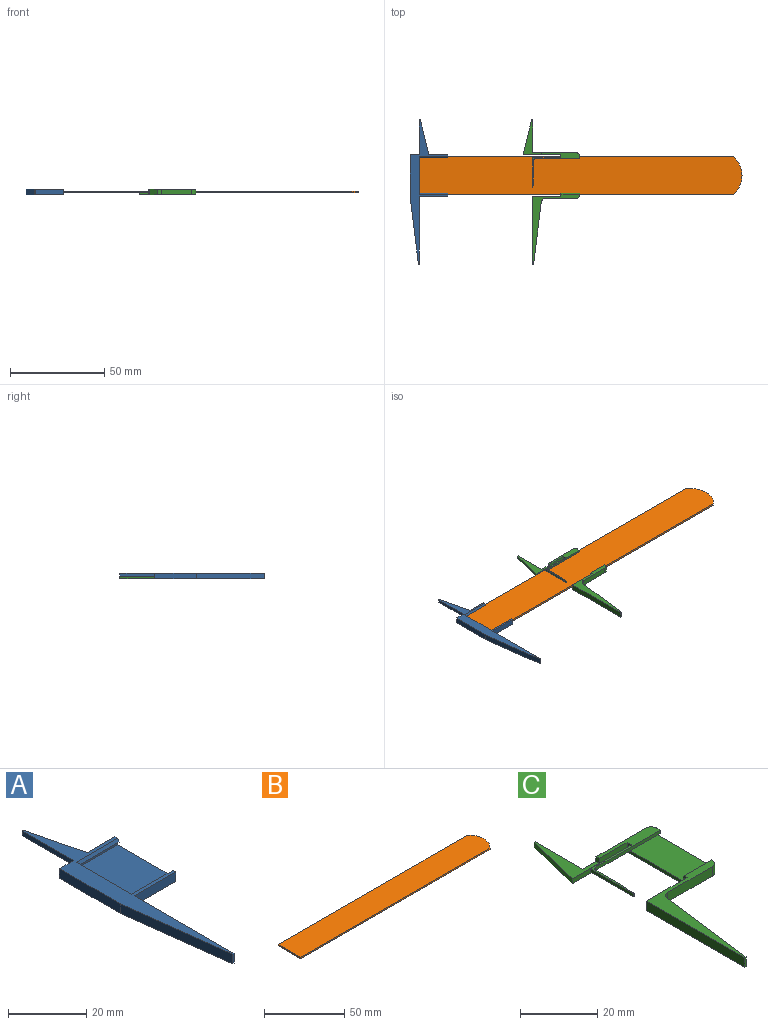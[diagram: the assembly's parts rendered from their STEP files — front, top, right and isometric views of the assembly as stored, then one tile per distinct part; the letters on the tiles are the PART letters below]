
ASSEMBLY  parts=3 mates=2
PART A: 21 faces, bbox 20x76.5x3 mm
  f0: plane 76.53x20mm, normal (0,0,1), area 289.2mm2, adj f2,f3,f4,f5,f6,f7,f8,f9
  f1: plane 58x20mm, normal (0,0,-1), area 539mm2, adj f2,f3,f4,f5,f6,f7,f11
  f2: plane 22x3mm, normal (-1,0,0), area 66mm2, adj f0,f1,f3,f11
  f3: plane 36x4.5mm, normal (-0.99,-0.12,0), area 108.8mm2, adj f0,f1,f2,f4
  f4: plane 3x0.5mm, normal (0,-1,0), area 1.5mm2, adj f0,f1,f3,f5
  f5: plane 36x3mm, normal (1,0,0), area 108mm2, adj f0,f1,f4,f6
  f6: plane 15x3mm, normal (0,-1,0), area 45mm2, adj f0,f1,f5,f7
  f7: plane 22x3mm, normal (1,0,0), area 26.3mm2, adj f0,f1,f6,f11,f14,f15,f16,f17
  f8: plane 18.53x4.49mm, normal (0.97,0.24,0), area 28.6mm2, adj f0,f9,f11,f12
  f9: plane 1.5x0.5mm, normal (0,1,0), area 0.8mm2, adj f0,f8,f10,f12
  f10: plane 18.53x1.5mm, normal (-1,0,0), area 27.8mm2, adj f0,f9,f11,f12
  f11: plane 20x3mm, normal (0,1,0), area 52.6mm2, adj f0,f1,f2,f7,f8,f10,f12
  f12: plane 18.53x4.99mm, normal (0,0,-1), area 50.5mm2, adj f8,f9,f10,f11
  f13: plane 20.02x2.01mm, normal (1,0,0), area 39.7mm2, adj f0,f14,f15,f16,f17,f18,f19,f20
  f14: plane 15x0.99mm, normal (0,0.89,0.45), area 16.6mm2, adj f0,f7,f13,f15
  f15: plane 15x0.5mm, normal (0,0,-1), area 7.5mm2, adj f7,f13,f14,f16
  f16: plane 15x1.02mm, normal (0,1,0), area 15.3mm2, adj f7,f13,f15,f17
  f17: plane 20.02x15mm, normal (0,0,1), area 300.3mm2, adj f7,f13,f16,f18
  f18: plane 15x1.02mm, normal (0,-1,0), area 15.3mm2, adj f7,f13,f17,f19
  f19: plane 15x0.5mm, normal (0,0,-1), area 7.5mm2, adj f7,f13,f18,f20
  f20: plane 15x0.99mm, normal (0,-0.89,0.45), area 16.6mm2, adj f0,f7,f13,f19
PART B: 6 faces, bbox 171x20x1 mm
  f0: cylinder r=13.36mm len=20mm, axis (0,0,-1), area 22.6mm2, adj f1,f3,f4,f5
  f1: plane 166.5x1mm, normal (0,1,0), area 166.5mm2, adj f0,f2,f4,f5
  f2: plane 20x1mm, normal (-1,0,0), area 20mm2, adj f1,f3,f4,f5
  f3: plane 166.5x1mm, normal (0,-1,0), area 166.5mm2, adj f0,f2,f4,f5
  f4: plane 171x20mm, normal (0,0,1), area 3392.4mm2, adj f0,f1,f2,f3
  f5: plane 171x20mm, normal (0,0,-1), area 3392.4mm2, adj f0,f1,f2,f3
PART C: 34 faces, bbox 30.1x76.5x3 mm
  f0: plane 24.99x18.56mm, normal (0,0,1), area 57.4mm2, adj f7,f8,f13,f14,f16,f25,f26,f27
  f1: plane 18.48x10.08mm, normal (0,0,1), area 56.8mm2, adj f8,f9,f10,f11,f13,f16
  f2: plane 76.53x30.08mm, normal (0,0,-1), area 420.9mm2, adj f3,f4,f5,f6,f7,f8,f9,f10
  f3: plane 35.95x3mm, normal (-1,0,0), area 107.8mm2, adj f2,f4,f12,f15
  f4: plane 3x0.5mm, normal (0,-1,0), area 1.5mm2, adj f2,f3,f5,f15
  f5: plane 33.05x4.14mm, normal (0.99,-0.12,0), area 99.9mm2, adj f2,f4,f15,f23
  f6: plane 16.37x3mm, normal (0,-1,0), area 49.1mm2, adj f2,f15,f23,f24
  f7: plane 20.37x3mm, normal (1,0,0), area 22.2mm2, adj f0,f2,f15,f17,f18,f19,f20,f21
  f8: plane 23.04x3mm, normal (0,1,0), area 62mm2, adj f0,f1,f2,f9,f16,f25
  f9: plane 17.37x1.5mm, normal (1,0,0), area 26mm2, adj f1,f2,f8,f10
  f10: plane 1.5x0.51mm, normal (0,1,0), area 0.8mm2, adj f1,f2,f9,f11
  f11: plane 18.48x4.53mm, normal (-0.97,0.24,0), area 28.5mm2, adj f1,f2,f10,f13
  f12: plane 15x3mm, normal (0,1,0), area 45mm2, adj f2,f3,f14,f15
  f13: plane 20.09x3mm, normal (0,-1,0), area 45.1mm2, adj f0,f1,f2,f11,f14,f16
  f14: plane 22.1x3mm, normal (-1,0,0), area 26.7mm2, adj f0,f2,f12,f13,f15,f17,f18,f19
  f15: plane 36.99x24.99mm, normal (0,0,1), area 132.2mm2, adj f3,f4,f5,f6,f7,f12,f14,f22
  f16: plane 1.5x1.12mm, normal (-0.97,-0.24,0), area 1.7mm2, adj f0,f1,f8,f13
  f17: plane 9.99x0.5mm, normal (0,0,-1), area 5mm2, adj f7,f14,f18,f22
  f18: plane 9.99x1.02mm, normal (0,1,0), area 10.2mm2, adj f7,f14,f17,f19
  f19: plane 20.02x9.99mm, normal (0,0,1), area 200mm2, adj f7,f14,f18,f20
  f20: plane 9.99x1.02mm, normal (0,-1,0), area 10.2mm2, adj f7,f14,f19,f21
  f21: plane 24.99x16.4mm, normal (0,0,-1), area 25.4mm2, adj f7,f14,f20,f26,f27,f28,f29,f30
  f22: plane 9.99x0.99mm, normal (0,0.89,0.45), area 11.1mm2, adj f7,f14,f15,f17
  f23: cylinder r=2mm len=3mm, axis (0,0,-1), area 8.7mm2, adj f2,f5,f6,f15
  f24: cylinder r=2mm len=3mm, axis (0,0,-1), area 9.4mm2, adj f2,f6,f7,f15
  f25: cylinder r=2mm len=3mm, axis (0,0,-1), area 9.4mm2, adj f0,f2,f7,f8
  f26: plane 23.49x0.99mm, normal (0,-1,0), area 23.3mm2, adj f0,f7,f21,f33
  f27: cylinder r=0.17mm len=0.99mm, axis (0,0,1), area 0.3mm2, adj f0,f14,f21,f28
  f28: plane 14.83x0.99mm, normal (0,1,0), area 14.7mm2, adj f0,f21,f27,f29
  f29: plane 15.79x0.99mm, normal (-1,0,0), area 15.6mm2, adj f0,f21,f28,f30
  f30: plane 0.99x0.17mm, normal (-0.06,-1,0), area 0.2mm2, adj f0,f21,f29,f31
  f31: plane 5.67x0.99mm, normal (1,-0.06,0), area 5.6mm2, adj f0,f21,f30,f32
  f32: plane 8.63x0.99mm, normal (1,0,0), area 8.5mm2, adj f0,f21,f31,f33
  f33: cylinder r=1mm len=1mm, axis (0,0,1), area 1.6mm2, adj f0,f21,f26,f32
PLACE A t=(9.88,0.98,0.66)mm
PLACE B t=(9.87,0.98,0.65)mm fixed
PLACE C t=(69.83,0.98,0.66)mm
MATE parallel A.f7 <-> C.f14  axis (1,0,0) through (4.88,0.98,0.15)mm
MATE fastened A.f13 <-> B.f2  axis (1,0,0) through (-10.12,0.98,0.15)mm
